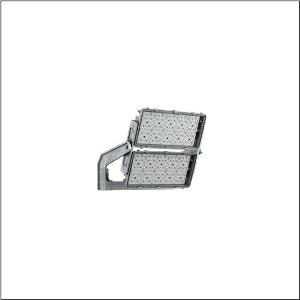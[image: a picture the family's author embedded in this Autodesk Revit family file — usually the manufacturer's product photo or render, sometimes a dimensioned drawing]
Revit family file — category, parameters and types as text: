
# Revit family: floodlight_fl_11_maxi_remote___rs12_5xa779514m01aa_cc46
name_source: partatom
category: Lighting Fixtures
units: mm (PartAtom-declared; Revit-internal decimal feet)

## family parameters
Cut with Voids When Loaded = No
Host = Face
Light Source = No
Part Type = Normal
Room Calculation Point = No
Round Connector Dimension = Use Diameter
Shared = No

## types (1)
- --- (1 x LED, 90180 lm, 916.8 W, 5700K)
    Apparent Load = 917 VA
    CIE Flux Codes = 79 92 99 100 100
    Color Rendering = 90
    Color Temperature = 5700K
    Default Elevation = 1800 mm
    Description = Floodlight FL 11  maxi  Remote floodlight; light control with lens of PMMA; cover panel of toughened safety glass, transparent; light distribution: RS12, rotationally symmetric direct distribution, LEDcolour temperature: 5700K, rated luminous flux: 90.180lm, colour rendering: CRI > 90, light colour: 957; luminous efficacy: 98lm/W; brightness control: DMX+RDM; with terminal, 6-pole, max. 2.5mm², mains connection: 220..240V/380..400V AC, 50/60Hz, surge voltage resistance: line to ground: 10kV, ECG replaceable separately, no afterglow with DALI off / DMX off command, LED unit replaceable without ESD environment, dustproof LED module, dimming range 10..100%; 917W floodlight with 2x LED unit of diecast aluminium, coated grey; length: 713mm / width: 651mm / height: 338mm; mounting bracket, of diecast aluminium, uncoated, natural, equipment: Power, protection rating (complete): IP66; insulation class (complete): insulation class I (protective earthing); certification: CE, ENEC, VDE; ball protection: ball impact resistance with accessories, impact resistance: IK07; rated ambient temperature 10°C, only for outdoor installations, permissible operating ambient temperature: -40..+30°C, permissible storage temperature: -40..+85°C; packaging unit: 1 piece

Light Distribution: RS12
    Height = 320 mm
    Lamp = 1 x LED
    Lamp Light Flux = 90180 lm
    Lamp Power = 916.8 W
    Lamp count = 1
    Length = 712 mm
    Luminous efficacy = 98 lm/W
    Manufacturer = Siteco
    ModVariant = No
    Model = 5XA779514M01AA
    Mounting Place = Ceiling
    Mounting Type = Surface mounted
    Number of Poles = 1
    OnlyDefault = Yes
    Power Factor = 1
    Product Name = Floodlight FL 11 maxi Remote | RS12
    Product group = floodlight | ceiling mounted
    ProductGroupID = 303
    Protection Class = Protection class I
    Protection Degree = IP 66
    RLX_Detail_Level = 1
    RLX_Emergency_Light_Flux = 0 lm
    RLX_Emergency_Type = 0
    RLX_Emergency_Type_DB = No
    RlxData = <blob elided: 41009 chars, md5=3af0f99a>
    Socket = socket
    Standby Power = 0 W
    System Light Flux = 90180 lm
    System Power = 917 W
    Type Comments = factory setting: luminous flux: 100 % | dim-lin: 254 | 950 mA
    Type Image = l_1006788.jpg
    URL = http://relux.com
    VarID = @adj_133539
    Voltage = 0 V
    Weight = 0.00 kg
    Width = 655 mm

## geometry (parser evidence)
native form markers: Blend x4, Sweep x15
no freeform markers — native parametric forms only
